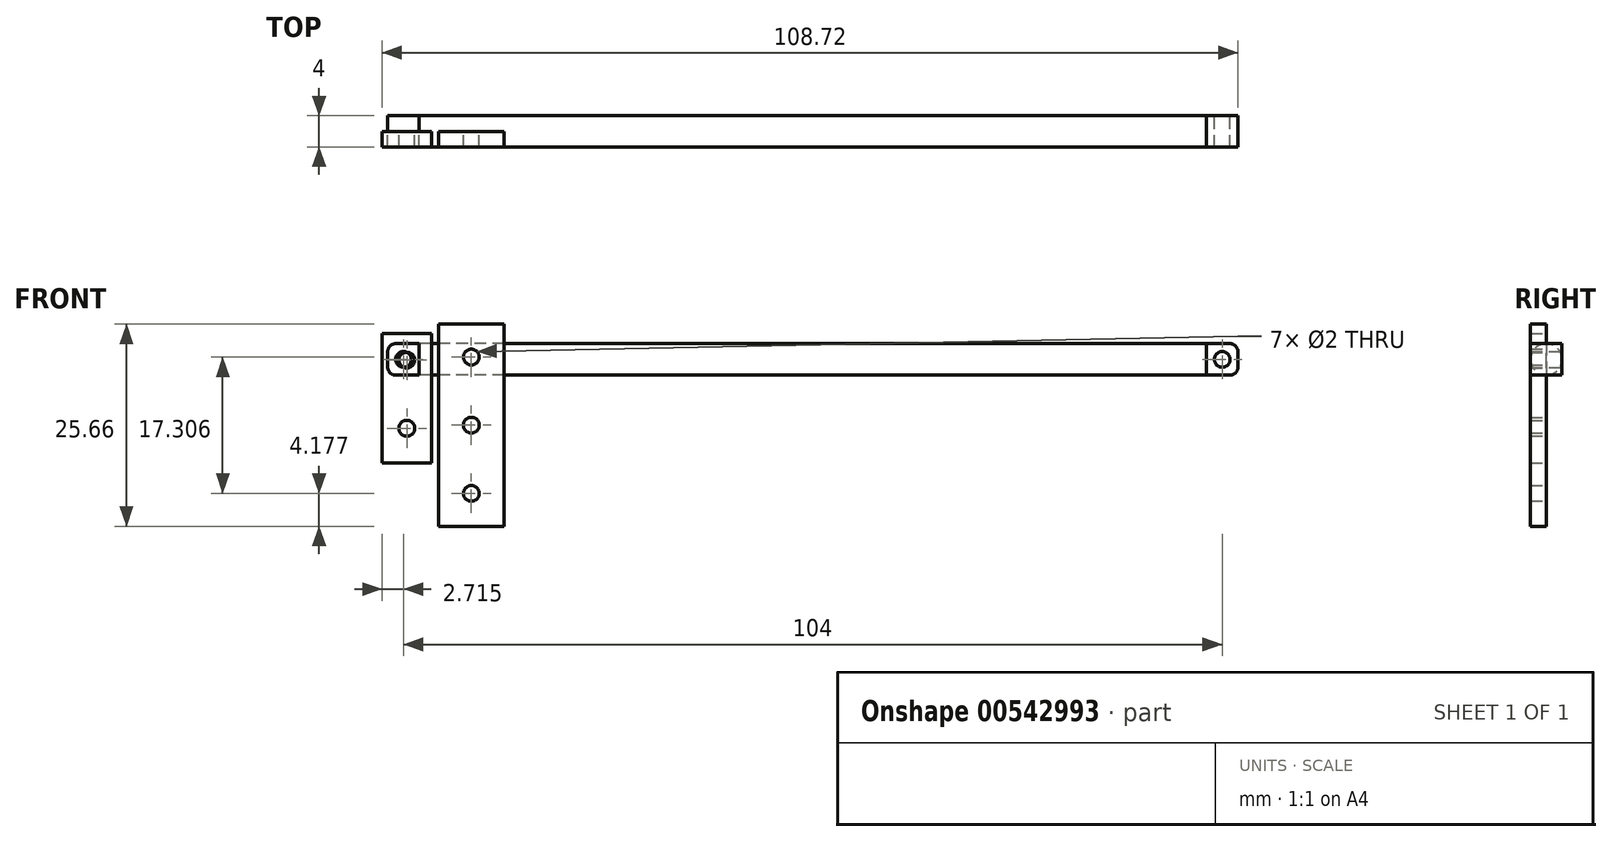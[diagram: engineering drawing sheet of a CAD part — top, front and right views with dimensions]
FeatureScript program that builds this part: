
annotation { "Feature Type Name" : "Feature", "Feature Type Description" : "" }
export const myFeature = defineFeature(function(context is Context, id is Id, definition is map)
    precondition{}
    {
        {
            var Q0;
            Q0=qCreatedBy(makeId("Front.planeOp"),FACE);
            var sketch = newSketch(context, id + "F0", { "sketchPlane" : qUnion([Q0])});
            skLineSegment(sketch, "E0.bottom", {"start": v(-56.3, 4.9) * mm, "end": v(43.7, 4.9) * mm});
            skLineSegment(sketch, "E0.top", {"start": v(-56.3, 2.9) * mm, "end": v(43.7, 2.9) * mm});
            skLineSegment(sketch, "E0.left", {"start": v(-56.3, 4.9) * mm, "end": v(-56.3, 2.9) * mm});
            skLineSegment(sketch, "E0.right", {"start": v(43.7, 4.9) * mm, "end": v(43.7, 2.9) * mm});
            skLineSegment(sketch, "E1.bottom", {"start": v(43.7, 4.9) * mm, "end": v(46.7, 4.9) * mm});
            skLineSegment(sketch, "E1.top", {"start": v(43.7, 0.9) * mm, "end": v(46.7, 0.9) * mm});
            skLineSegment(sketch, "E1.left", {"start": v(43.7, 4.9) * mm, "end": v(43.7, 0.9) * mm});
            skLineSegment(sketch, "E1.right", {"start": v(47.7, 3.9) * mm, "end": v(47.7, 1.9) * mm});
            skLineSegment(sketch, "E2.bottom", {"start": v(-59.3, 4.9) * mm, "end": v(-56.3, 4.9) * mm});
            skLineSegment(sketch, "E2.top", {"start": v(-59.3, 0.9) * mm, "end": v(-56.3, 0.9) * mm});
            skLineSegment(sketch, "E2.left", {"start": v(-60.3, 3.9) * mm, "end": v(-60.3, 1.9) * mm});
            skLineSegment(sketch, "E2.right", {"start": v(-56.3, 4.9) * mm, "end": v(-56.3, 0.9) * mm});
            skPoint(sketch, "E3.visualSharp", {"position": v(-60.3, 4.9) * mm});
            skArc(sketch, "E3.filletArc", {"start": v(-59.3, 4.9) * mm, "mid": v(-60.01, 4.6) * mm, "end": v(-60.3, 3.9) * mm});
            skPoint(sketch, "E4.visualSharp", {"position": v(-60.4, 0.9) * mm});
            skArc(sketch, "E4.filletArc", {"start": v(-60.3, 1.9) * mm, "mid": v(-60.01, 1.18) * mm, "end": v(-59.3, 0.9) * mm});
            skCircle(sketch, "E5", {"center": v(-58.3, 2.9) * mm, "radius": 1 * mm});
            skCircle(sketch, "E6", {"center": v(45.7, 2.9) * mm, "radius": 1 * mm});
            skLineSegment(sketch, "E7", {"start": v(-58.3, 2.9) * mm, "end": v(-56.3, 2.9) * mm, "construction": true});
            skLineSegment(sketch, "E8", {"start": v(-60.3, 2.9) * mm, "end": v(-58.3, 2.9) * mm, "construction": true});
            skLineSegment(sketch, "E9", {"start": v(45.7, 2.9) * mm, "end": v(43.7, 2.9) * mm, "construction": true});
            skLineSegment(sketch, "E10", {"start": v(45.7, 2.9) * mm, "end": v(47.7, 2.9) * mm, "construction": true});
            skLineSegment(sketch, "E11", {"start": v(45.7, 2.9) * mm, "end": v(45.7, 4.9) * mm, "construction": true});
            skPoint(sketch, "E12.visualSharp", {"position": v(47.7, 0.9) * mm});
            skArc(sketch, "E12.filletArc", {"start": v(46.7, 0.9) * mm, "mid": v(47.4, 1.18) * mm, "end": v(47.7, 1.9) * mm});
            skPoint(sketch, "E13.visualSharp", {"position": v(47.7, 4.9) * mm});
            skArc(sketch, "E13.filletArc", {"start": v(47.7, 3.9) * mm, "mid": v(47.4, 4.6) * mm, "end": v(46.7, 4.9) * mm});
            skSolve(sketch);
        }
        {
            var Q0;
            {var subQ0=sQuery(id+"F0.wireOp",EDGE,"E0.bottom");Q0=makeQuery(id+"F0.imprint","IMPRINT",FACE,{"disambiguationData":[TD([[makeQuery(id+"F0.imprint","IMPRINT",EDGE,{"derivedFrom":subQ0}),-1.0]])]});}
            var Q1;
            Q1=sQuery(id+"F0.wireOp",EDGE,"E0.top");
            revolve(context, id + "F1", {"entities" : qUnion([Q0]), "axis" : qUnion([Q1]), "revolveType" : RevolveType.FULL});
        }
        {
            var Q0;
            {var subQ2=sQuery(id+"F0.wireOp",EDGE,"E2.bottom");Q0=makeQuery(id+"F0.imprint","IMPRINT",FACE,{"disambiguationData":[TD([[makeQuery(id+"F0.imprint","IMPRINT",EDGE,{"derivedFrom":subQ2}),-1.0]])]});}
            var Q1;
            {var subQ3=sQuery(id+"F0.wireOp",EDGE,"E1.bottom");Q1=makeQuery(id+"F0.imprint","IMPRINT",FACE,{"disambiguationData":[TD([[makeQuery(id+"F0.imprint","IMPRINT",EDGE,{"derivedFrom":subQ3}),-1.0]])]});}
            extrude(context, id + "F2", {"entities" : qUnion([Q0, Q1]), "operationType" : NewBodyOperationType.ADD, "endBound" : BoundingType.SYMMETRIC, "depth" : 4 * mm, "offsetDistance" : 25.4 * mm});
        }
        {
            var Q0;
            Q0=qCreatedBy(makeId("Front.planeOp"),FACE);
            var sketch = newSketch(context, id + "F3", { "sketchPlane" : qUnion([Q0])});
            skLineSegment(sketch, "E14.bottom", {"start": v(-61.02, 6.2) * mm, "end": v(-54.74, 6.2) * mm});
            skLineSegment(sketch, "E14.top", {"start": v(-61.02, -10.24) * mm, "end": v(-54.74, -10.24) * mm});
            skLineSegment(sketch, "E14.left", {"start": v(-61.02, 6.2) * mm, "end": v(-61.02, -10.24) * mm});
            skLineSegment(sketch, "E14.right", {"start": v(-54.74, 6.2) * mm, "end": v(-54.74, -10.24) * mm});
            skCircle(sketch, "E15", {"center": v(-57.88, 2.8) * mm, "radius": 1 * mm});
            skCircle(sketch, "E16", {"center": v(-57.88, -5.86) * mm, "radius": 1 * mm});
            skLineSegment(sketch, "E17", {"start": v(-57.88, 2.8) * mm, "end": v(-57.88, -5.86) * mm, "construction": true});
            skLineSegment(sketch, "E18", {"start": v(-61.02, -5.86) * mm, "end": v(-57.88, -5.86) * mm, "construction": true});
            skLineSegment(sketch, "E19", {"start": v(-57.88, -5.86) * mm, "end": v(-54.74, -5.86) * mm, "construction": true});
            skSolve(sketch);
        }
        {
            var Q0;
            Q0=makeQuery(id+"F3.imprint","IMPRINT",FACE,{"disambiguationData":[TD([[makeQuery(id+"F3.imprint","IMPRINT",EDGE,{"derivedFrom":sQuery(id+"F3.wireOp",EDGE,"E14.bottom")}),-1.0]])]});
            var Q1;
            Q1 = qConstructionFilter(qBodyType(qCreatedBy(id + "F3" ,EDGE), BodyType.WIRE), ConstructionObject.NO);
            extrude(context, id + "F4", {"entities" : qUnion([Q0]), "surfaceEntities" : qUnion([Q1]), "depth" : 2 * mm, "offsetDistance" : 25 * mm});
        }
        {
            var Q0;
            Q0=qCreatedBy(makeId("Front.planeOp"),FACE);
            var sketch = newSketch(context, id + "F5", { "sketchPlane" : qUnion([Q0])});
            skLineSegment(sketch, "E20.bottom", {"start": v(-53.87, 7.36) * mm, "end": v(-45.5, 7.36) * mm});
            skLineSegment(sketch, "E20.top", {"start": v(-53.87, -18.3) * mm, "end": v(-45.5, -18.3) * mm});
            skLineSegment(sketch, "E20.left", {"start": v(-53.87, 7.36) * mm, "end": v(-53.87, -18.3) * mm});
            skLineSegment(sketch, "E20.right", {"start": v(-45.5, 7.36) * mm, "end": v(-45.5, -18.3) * mm});
            skCircle(sketch, "E21", {"center": v(-49.69, 3.18) * mm, "radius": 1 * mm});
            skCircle(sketch, "E22", {"center": v(-49.69, -5.47) * mm, "radius": 1 * mm});
            skCircle(sketch, "E23", {"center": v(-49.69, -14.12) * mm, "radius": 1 * mm});
            skLineSegment(sketch, "E24", {"start": v(-49.69, 3.18) * mm, "end": v(-49.69, -5.47) * mm, "construction": true});
            skLineSegment(sketch, "E25", {"start": v(-49.69, -5.47) * mm, "end": v(-49.69, -14.12) * mm, "construction": true});
            skLineSegment(sketch, "E26", {"start": v(-45.5, 3.22) * mm, "end": v(-49.69, 3.18) * mm, "construction": true});
            skLineSegment(sketch, "E27", {"start": v(-49.69, 3.18) * mm, "end": v(-53.87, 3.18) * mm, "construction": true});
            skLineSegment(sketch, "E28", {"start": v(-49.69, 3.18) * mm, "end": v(-49.73, 7.36) * mm, "construction": true});
            skLineSegment(sketch, "E29", {"start": v(-49.69, -14.12) * mm, "end": v(-49.69, -18.3) * mm, "construction": true});
            skSolve(sketch);
        }
        {
            var Q0;
            Q0 = qSketchRegion(id + "F5", true);
            var Q1;
            Q1=sQuery(id+"F5.wireOp",EDGE,"E22");
            extrude(context, id + "F6", {"entities" : qUnion([Q0]), "surfaceEntities" : qUnion([Q1]), "depth" : 2 * mm, "offsetDistance" : 25 * mm});
        }
    });
